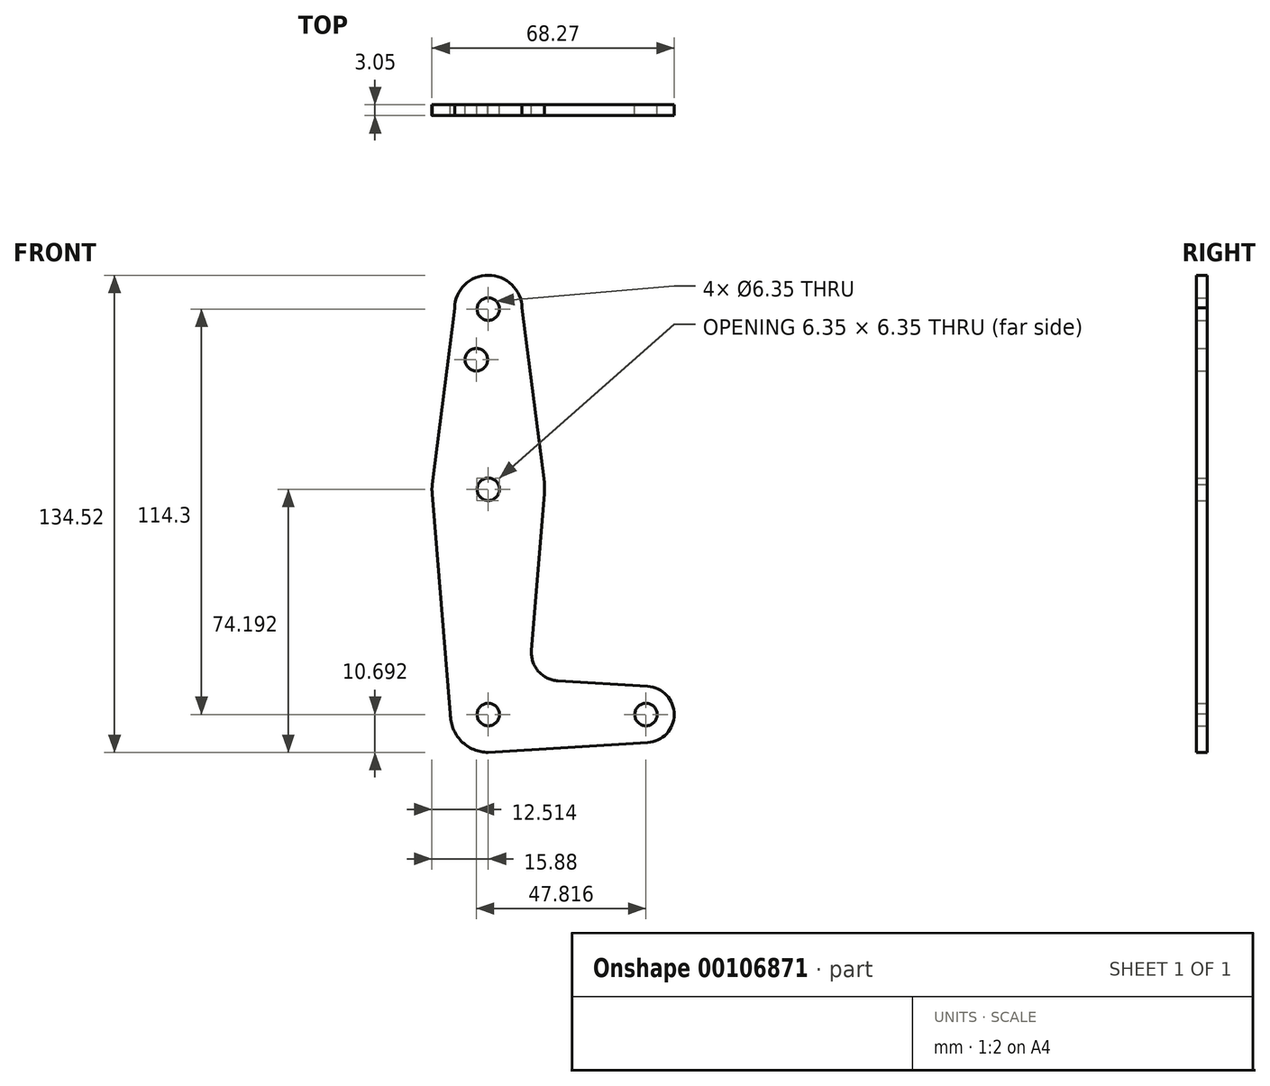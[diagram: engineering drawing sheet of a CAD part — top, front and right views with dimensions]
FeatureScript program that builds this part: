
annotation { "Feature Type Name" : "Feature", "Feature Type Description" : "" }
export const myFeature = defineFeature(function(context is Context, id is Id, definition is map)
    precondition{}
    {
        {
            var Q0;
            Q0=qCreatedBy(makeId("Front.planeOp"),FACE);
            var sketch = newSketch(context, id + "F0", { "sketchPlane" : qUnion([Q0])});
            skLineSegment(sketch, "E0", {"start": v(0, -53.65) * mm, "end": v(44.45, -53.65) * mm});
            skCircle(sketch, "E1", {"center": v(0, 60.65) * mm, "radius": 9.53 * mm});
            skCircle(sketch, "E2", {"center": v(0, 9.85) * mm, "radius": 15.88 * mm});
            skCircle(sketch, "E3", {"center": v(44.45, -53.65) * mm, "radius": 7.94 * mm});
            skCircle(sketch, "E4", {"center": v(0, -53.65) * mm, "radius": 10.7 * mm});
            skLineSegment(sketch, "E5", {"start": v(0, -53.65) * mm, "end": v(0, 60.65) * mm});
            skLineSegment(sketch, "E6", {"start": v(0, -64.34) * mm, "end": v(44.94, -61.57) * mm});
            skLineSegment(sketch, "E7", {"start": v(19.62, -44.16) * mm, "end": v(44.94, -45.73) * mm});
            skLineSegment(sketch, "E8", {"start": v(12.18, -35.58) * mm, "end": v(15.82, 8.55) * mm});
            skLineSegment(sketch, "E9", {"start": v(-10.7, -53.47) * mm, "end": v(-15.82, 8.55) * mm});
            skLineSegment(sketch, "E10", {"start": v(-9.52, 60.93) * mm, "end": v(-15.82, 11.16) * mm});
            skLineSegment(sketch, "E11", {"start": v(9.52, 60.95) * mm, "end": v(15.75, 11.85) * mm});
            skCircle(sketch, "E12", {"center": v(0, 60.65) * mm, "radius": 3.18 * mm});
            skCircle(sketch, "E13", {"center": v(0, 9.85) * mm, "radius": 3.18 * mm});
            skCircle(sketch, "E14", {"center": v(0, -53.65) * mm, "radius": 3.18 * mm});
            skCircle(sketch, "E15", {"center": v(44.45, -53.65) * mm, "radius": 3.18 * mm});
            skCircle(sketch, "E16", {"center": v(-3.37, 46.38) * mm, "radius": 3.18 * mm});
            skArc(sketch, "E17.filletArc", {"start": v(12.18, -35.58) * mm, "mid": v(14.1, -41.43) * mm, "end": v(19.62, -44.16) * mm});
            skSolve(sketch);
        }
        {
            var Q0;
            {var subQ0=sQuery(id+"F0.wireOp",EDGE,"E7");Q0=makeQuery(id+"F0.imprint","IMPRINT",FACE,{"disambiguationData":[TD([[makeQuery(id+"F0.imprint","IMPRINT",EDGE,{"derivedFrom":subQ0}),-1.0]])]});}
            var Q1;
            {var subQ0=sQuery(id+"F0.wireOp",EDGE,"E9");Q1=makeQuery(id+"F0.imprint","IMPRINT",FACE,{"disambiguationData":[TD([[makeQuery(id+"F0.imprint","IMPRINT",EDGE,{"derivedFrom":subQ0}),-1.0]])]});}
            var Q2;
            {var subQ3=sQuery(id+"F0.wireOp",EDGE,"E0");var subQ9=sQuery(id+"F0.wireOp",EDGE,"E14");var subQ10=makeQuery(id+"F0.imprint","INTERSECT",VERTEX,{"derivedFrom":[subQ3,subQ9]});Q2=makeQuery(id+"F0.imprint","IMPRINT",FACE,{"disambiguationData":[TD([[makeQuery(id+"F0.imprint","IMPRINT",EDGE,{"disambiguationData":[TD([[subQ10,-1.0]])],"derivedFrom":subQ3}),-1.0]])]});}
            var Q3;
            {var subQ0=sQuery(id+"F0.wireOp",EDGE,"E14");var subQ1=sQuery(id+"F0.wireOp",EDGE,"E0");var subQ2=makeQuery(id+"F0.imprint","INTERSECT",VERTEX,{"derivedFrom":[subQ1,subQ0]});Q3=makeQuery(id+"F0.imprint","IMPRINT",FACE,{"disambiguationData":[TD([[makeQuery(id+"F0.imprint","IMPRINT",EDGE,{"disambiguationData":[TD([[subQ2,-1.0]])],"derivedFrom":subQ1}),1.0]])]});}
            var Q4;
            {var subQ0=sQuery(id+"F0.wireOp",EDGE,"E3");var subQ1=sQuery(id+"F0.wireOp",EDGE,"E0");var subQ2=makeQuery(id+"F0.imprint","INTERSECT",VERTEX,{"derivedFrom":[subQ1,subQ0]});Q4=makeQuery(id+"F0.imprint","IMPRINT",FACE,{"disambiguationData":[TD([[makeQuery(id+"F0.imprint","IMPRINT",EDGE,{"disambiguationData":[TD([[subQ2,1.0]])],"derivedFrom":subQ1}),-1.0]])]});}
            var Q5;
            Q5=makeQuery(id+"F0.imprint","IMPRINT",FACE,{"disambiguationData":[TD([[makeQuery(id+"F0.imprint","IMPRINT",EDGE,{"derivedFrom":sQuery(id+"F0.wireOp",EDGE,"E15")}),-1.0]])]});
            var Q6;
            {var subQ1=sQuery(id+"F0.wireOp",EDGE,"E2");var subQ7=sQuery(id+"F0.wireOp",EDGE,"E10");var subQ9=makeQuery(id+"F0.imprint","INTERSECT",VERTEX,{"disambiguationData":[OD(1.0)],"derivedFrom":[subQ1,subQ7]});Q6=makeQuery(id+"F0.imprint","IMPRINT",FACE,{"disambiguationData":[TD([[makeQuery(id+"F0.imprint","IMPRINT",EDGE,{"disambiguationData":[TD([[subQ9,1.0]])],"derivedFrom":subQ1}),1.0]])]});}
            var Q7;
            {var subQ0=sQuery(id+"F0.wireOp",EDGE,"E2");var subQ2=makeQuery(id+"F0.imprint","INTERSECT",VERTEX,{"derivedFrom":[subQ0,sQuery(id+"F0.wireOp",EDGE,"E11")]});Q7=makeQuery(id+"F0.imprint","IMPRINT",FACE,{"disambiguationData":[TD([[makeQuery(id+"F0.imprint","IMPRINT",EDGE,{"disambiguationData":[TD([[subQ2,-1.0]])],"derivedFrom":subQ0}),1.0]])]});}
            var Q8;
            {var subQ0=sQuery(id+"F0.wireOp",EDGE,"E11");Q8=makeQuery(id+"F0.imprint","IMPRINT",FACE,{"disambiguationData":[TD([[makeQuery(id+"F0.imprint","IMPRINT",EDGE,{"derivedFrom":subQ0}),-1.0]])]});}
            var Q9;
            Q9=makeQuery(id+"F0.imprint","IMPRINT",FACE,{"disambiguationData":[TD([[makeQuery(id+"F0.imprint","IMPRINT",EDGE,{"derivedFrom":sQuery(id+"F0.wireOp",EDGE,"E16")}),-1.0]])]});
            var Q10;
            Q10=makeQuery(id+"F0.imprint","IMPRINT",FACE,{"disambiguationData":[TD([[makeQuery(id+"F0.imprint","IMPRINT",EDGE,{"derivedFrom":sQuery(id+"F0.wireOp",EDGE,"E12")}),-1.0]])]});
            extrude(context, id + "F1", {"entities" : qUnion([Q0, Q1, Q2, Q3, Q4, Q5, Q6, Q7, Q8, Q9, Q10]), "depth" : 3.05 * mm});
        }
    });
